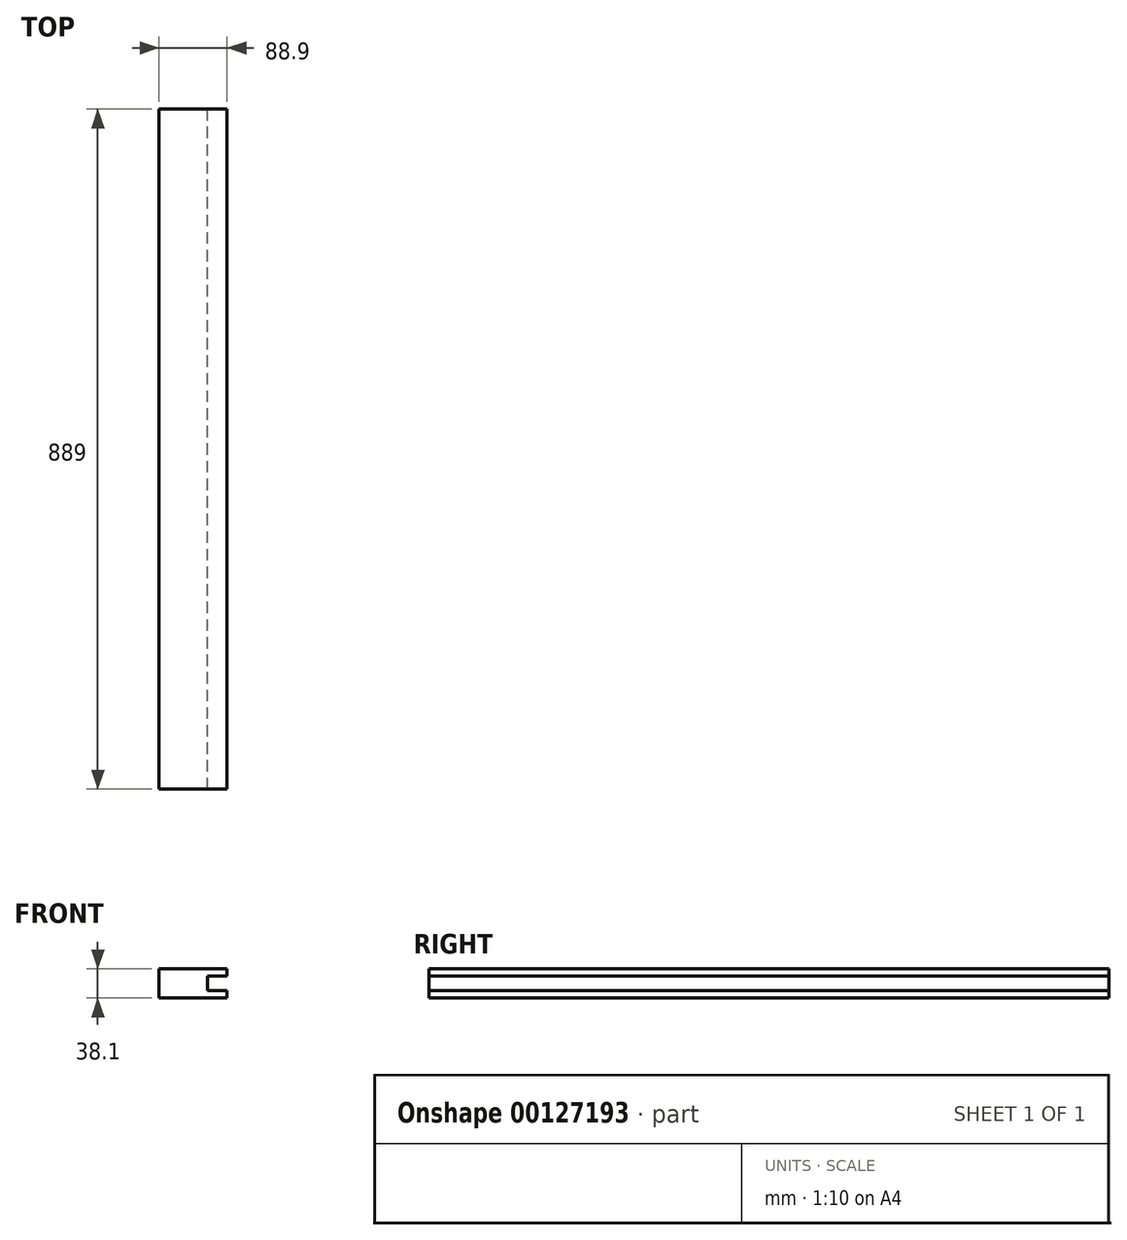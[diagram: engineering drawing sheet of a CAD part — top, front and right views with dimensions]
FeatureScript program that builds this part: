
annotation { "Feature Type Name" : "Feature", "Feature Type Description" : "" }
export const myFeature = defineFeature(function(context is Context, id is Id, definition is map)
    precondition{}
    {
        {
            var Q0;
            Q0=qCreatedBy(makeId("Front.planeOp"),FACE);
            var sketch = newSketch(context, id + "F0", { "sketchPlane" : qUnion([Q0])});
            skLineSegment(sketch, "E0.bottom", {"start": v(44.45, -19.05) * mm, "end": v(-44.45, -19.05) * mm});
            skLineSegment(sketch, "E0.top", {"start": v(44.45, 19.05) * mm, "end": v(-44.45, 19.05) * mm});
            skLineSegment(sketch, "E0.right", {"start": v(-44.45, -19.05) * mm, "end": v(-44.45, 19.05) * mm});
            skPoint(sketch, "E0.middle", {"position": v(0, 0) * mm});
            skLineSegment(sketch, "E1.top", {"start": v(44.45, -9.52) * mm, "end": v(19.05, -9.52) * mm});
            skLineSegment(sketch, "E1.right", {"start": v(19.05, 0) * mm, "end": v(19.05, -9.52) * mm});
            skLineSegment(sketch, "E2.top", {"start": v(44.45, 9.53) * mm, "end": v(19.05, 9.53) * mm});
            skLineSegment(sketch, "E2.right", {"start": v(19.05, 0) * mm, "end": v(19.05, 9.53) * mm});
            skLineSegment(sketch, "E3", {"start": v(44.45, 9.53) * mm, "end": v(44.45, 19.05) * mm});
            skLineSegment(sketch, "E4", {"start": v(44.45, -9.52) * mm, "end": v(44.45, -19.05) * mm});
            skSolve(sketch);
        }
        {
            var Q0;
            Q0=qSketchRegion(id+"F0",true);
            extrude(context, id + "F1", {"entities" : qUnion([Q0]), "depth" : 889 * mm, "offsetDistance" : 25.4 * mm});
        }
    });
